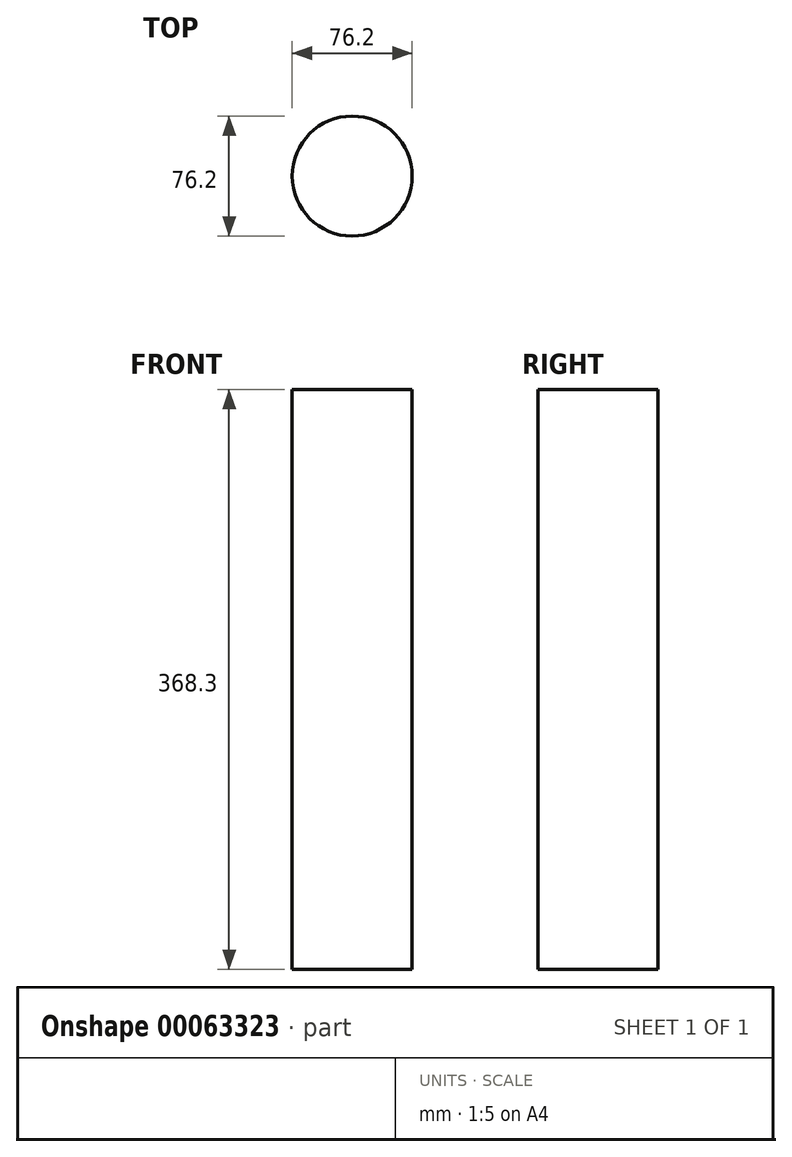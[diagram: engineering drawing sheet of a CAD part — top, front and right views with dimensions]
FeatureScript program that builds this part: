
annotation { "Feature Type Name" : "Feature", "Feature Type Description" : "" }
export const myFeature = defineFeature(function(context is Context, id is Id, definition is map)
    precondition{}
    {
        {
            var Q0;
            Q0=qCreatedBy(makeId("Front.planeOp"),FACE);
            var sketch = newSketch(context, id + "F0", { "sketchPlane" : qUnion([Q0])});
            skLineSegment(sketch, "E0.bottom", {"start": v(0, 209.14) * mm, "end": v(38.1, 209.14) * mm});
            skLineSegment(sketch, "E0.top", {"start": v(0, -159.16) * mm, "end": v(38.1, -159.16) * mm});
            skLineSegment(sketch, "E0.left", {"start": v(0, 209.14) * mm, "end": v(0, -159.16) * mm});
            skLineSegment(sketch, "E0.right", {"start": v(38.1, 209.14) * mm, "end": v(38.1, -159.16) * mm});
            skSolve(sketch);
        }
        {
            var Q0;
            Q0=qCreatedBy(makeId("Front.planeOp"),FACE);
            var sketch = newSketch(context, id + "F1", { "sketchPlane" : qUnion([Q0])});
            skLineSegment(sketch, "E1", {"start": v(0, 69.63) * mm, "end": v(0, -62.65) * mm, "construction": true});
            skSolve(sketch);
        }
        {
            var Q0;
            Q0=makeQuery(id+"F0.imprint","IMPRINT",FACE,{"disambiguationData":[TD([[makeQuery(id+"F0.imprint","IMPRINT",EDGE,{"derivedFrom":sQuery(id+"F0.wireOp",EDGE,"E0.bottom")}),-1.0]])]});
            var Q1;
            Q1=sQuery(id+"F1.wireOp",EDGE,"E1");
            revolve(context, id + "F2", {"entities" : qUnion([Q0]), "axis" : qUnion([Q1]), "revolveType" : RevolveType.FULL});
        }
    });
